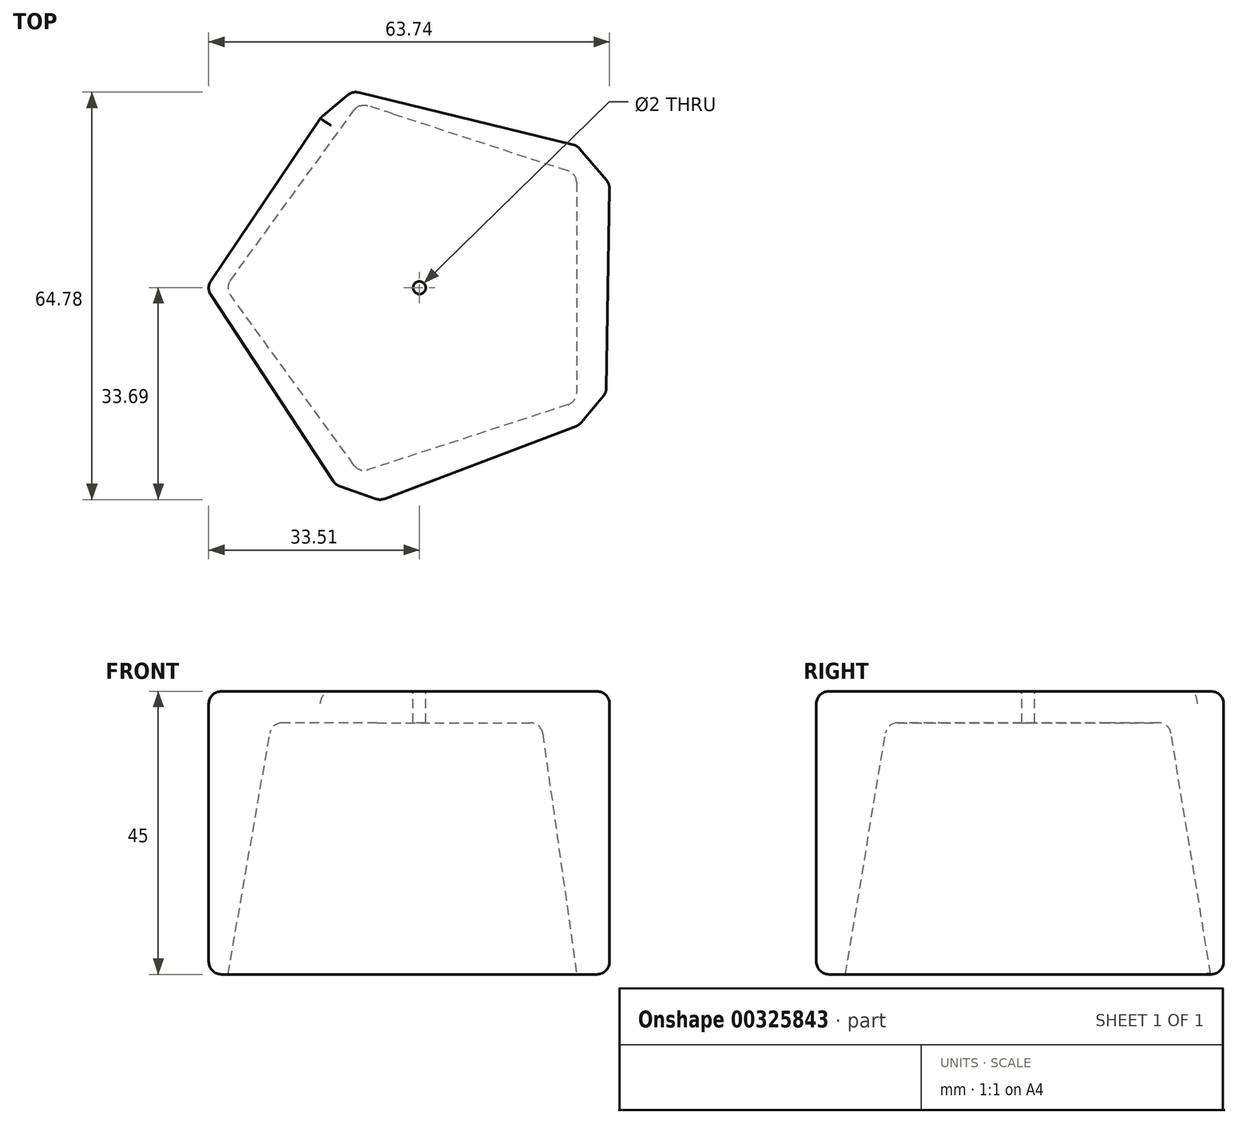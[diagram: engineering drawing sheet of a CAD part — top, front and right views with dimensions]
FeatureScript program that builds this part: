
annotation { "Feature Type Name" : "Feature", "Feature Type Description" : "" }
export const myFeature = defineFeature(function(context is Context, id is Id, definition is map)
    precondition{}
    {
        {
            var Q0;
            Q0=qCreatedBy(makeId("Top.planeOp"),FACE);
            var sketch = newSketch(context, id + "F0", { "sketchPlane" : qUnion([Q0])});
            skLineSegment(sketch, "E0", {"start": v(30.24, 16.51) * mm, "end": v(25.06, 22.6) * mm});
            skLineSegment(sketch, "E1", {"start": v(25.06, 22.6) * mm, "end": v(-10.67, 31.28) * mm});
            skLineSegment(sketch, "E2", {"start": v(-6.22, -33.82) * mm, "end": v(25.44, -21.81) * mm});
            skLineSegment(sketch, "E3", {"start": v(25.44, -21.81) * mm, "end": v(29.72, -16.68) * mm});
            skLineSegment(sketch, "E4", {"start": v(29.72, -16.68) * mm, "end": v(30.24, 16.51) * mm});
            skLineSegment(sketch, "E5", {"start": v(-10.67, 31.28) * mm, "end": v(-15.57, 27.15) * mm});
            skLineSegment(sketch, "E6", {"start": v(-15.57, 27.15) * mm, "end": v(-33.91, 0) * mm});
            skLineSegment(sketch, "E7", {"start": v(-33.91, 0) * mm, "end": v(-13.36, -31.31) * mm});
            skLineSegment(sketch, "E8", {"start": v(-13.36, -31.31) * mm, "end": v(-6.22, -33.82) * mm});
            skSolve(sketch);
        }
        {
            var Q0;
            Q0 = qSketchRegion(id + "F0", true);
            extrude(context, id + "F1", {"entities" : qUnion([Q0]), "depth" : 45 * mm});
        }
        {
            var Q0;
            Q0=qCreatedBy(makeId("Top.planeOp"),FACE);
            var sketch = newSketch(context, id + "F2", { "sketchPlane" : qUnion([Q0])});
            skCircle(sketch, "E9.cCircle", {"center": v(0, 0) * mm, "radius": 25 * mm, "construction": true});
            skLineSegment(sketch, "E9.0", {"start": v(25, 18.16) * mm, "end": v(25, -18.16) * mm});
            skLineSegment(sketch, "E9.1", {"start": v(25, -18.16) * mm, "end": v(-9.55, -29.39) * mm});
            skLineSegment(sketch, "E9.2", {"start": v(-9.55, -29.39) * mm, "end": v(-30.9, 0) * mm});
            skLineSegment(sketch, "E9.3", {"start": v(-30.9, 0) * mm, "end": v(-9.55, 29.39) * mm});
            skLineSegment(sketch, "E9.4", {"start": v(-9.55, 29.39) * mm, "end": v(25, 18.16) * mm});
            skPoint(sketch, "E9.0.midPoint", {"position": v(25, 0) * mm});
            skSolve(sketch);
        }
        {
            var Q0;
            Q0 = qSketchRegion(id + "F2", true);
            extrude(context, id + "F3", {"entities" : qUnion([Q0]), "operationType" : NewBodyOperationType.REMOVE, "depth" : 40 * mm, "hasDraft" : true, "draftAngle" : 8 * degree, "draftPullDirection" : true});
        }
        {
            var Q0;
            Q0=makeQuery(id+"F3.boolean.opBoolean","COPY",EDGE,{"derivedFrom":makeQuery(id+"F3.opExtrude","CAP_EDGE",EDGE,{"disambiguationData":[OSD([sQuery(id+"F2.wireOp",EDGE,"E9.4")])],"isStart":false})});
            var Q1;
            Q1=makeQuery(id+"F3.boolean.opBoolean","COPY",EDGE,{"derivedFrom":makeQuery(id+"F3.opExtrude","SWEPT_EDGE",EDGE,{"disambiguationData":[OSD([sQuery(id+"F2.wireOp",EDGE,"E9.0"),sQuery(id+"F2.wireOp",EDGE,"E9.4")])]})});
            var Q2;
            Q2=makeQuery(id+"F3.boolean.opBoolean","COPY",EDGE,{"derivedFrom":makeQuery(id+"F3.opExtrude","CAP_EDGE",EDGE,{"disambiguationData":[OSD([sQuery(id+"F2.wireOp",EDGE,"E9.0")])],"isStart":false})});
            var Q3;
            Q3=makeQuery(id+"F3.boolean.opBoolean","COPY",EDGE,{"derivedFrom":makeQuery(id+"F3.opExtrude","CAP_EDGE",EDGE,{"disambiguationData":[OSD([sQuery(id+"F2.wireOp",EDGE,"E9.1")])],"isStart":false})});
            var Q4;
            Q4=makeQuery(id+"F3.boolean.opBoolean","COPY",EDGE,{"derivedFrom":makeQuery(id+"F3.opExtrude","CAP_EDGE",EDGE,{"disambiguationData":[OSD([sQuery(id+"F2.wireOp",EDGE,"E9.2")])],"isStart":false})});
            var Q5;
            Q5=makeQuery(id+"F3.boolean.opBoolean","COPY",EDGE,{"derivedFrom":makeQuery(id+"F3.opExtrude","CAP_EDGE",EDGE,{"disambiguationData":[OSD([sQuery(id+"F2.wireOp",EDGE,"E9.3")])],"isStart":false})});
            var Q6;
            Q6=makeQuery(id+"F3.boolean.opBoolean","COPY",EDGE,{"derivedFrom":makeQuery(id+"F3.opExtrude","SWEPT_EDGE",EDGE,{"disambiguationData":[OSD([sQuery(id+"F2.wireOp",EDGE,"E9.3"),sQuery(id+"F2.wireOp",EDGE,"E9.4")])]})});
            var Q7;
            Q7=makeQuery(id+"F3.boolean.opBoolean","COPY",EDGE,{"derivedFrom":makeQuery(id+"F3.opExtrude","SWEPT_EDGE",EDGE,{"disambiguationData":[OSD([sQuery(id+"F2.wireOp",EDGE,"E9.2"),sQuery(id+"F2.wireOp",EDGE,"E9.3")])]})});
            var Q8;
            Q8=makeQuery(id+"F3.boolean.opBoolean","COPY",EDGE,{"derivedFrom":makeQuery(id+"F3.opExtrude","SWEPT_EDGE",EDGE,{"disambiguationData":[OSD([sQuery(id+"F2.wireOp",EDGE,"E9.1"),sQuery(id+"F2.wireOp",EDGE,"E9.2")])]})});
            var Q9;
            Q9=makeQuery(id+"F3.boolean.opBoolean","COPY",EDGE,{"derivedFrom":makeQuery(id+"F3.opExtrude","SWEPT_EDGE",EDGE,{"disambiguationData":[OSD([sQuery(id+"F2.wireOp",EDGE,"E9.0"),sQuery(id+"F2.wireOp",EDGE,"E9.1")])]})});
            fillet(context, id + "F4", {"entities" : qUnion([Q0, Q1, Q2, Q3, Q4, Q5, Q6, Q7, Q8, Q9]), "radius" : 2 * mm, "tangentPropagation" : true, "allowEdgeOverflow" : false});
        }
        {
            var Q0;
            Q0=makeQuery(id+"F1.opExtrude","SWEPT_FACE",FACE,{"disambiguationData":[OSD([sQuery(id+"F0.wireOp",EDGE,"E1")])]});
            var Q1;
            Q1=makeQuery(id+"F1.opExtrude","SWEPT_FACE",FACE,{"disambiguationData":[OSD([sQuery(id+"F0.wireOp",EDGE,"E0")])]});
            var Q2;
            Q2=makeQuery(id+"F1.opExtrude","SWEPT_FACE",FACE,{"disambiguationData":[OSD([sQuery(id+"F0.wireOp",EDGE,"E4")])]});
            var Q3;
            Q3=makeQuery(id+"F1.opExtrude","SWEPT_FACE",FACE,{"disambiguationData":[OSD([sQuery(id+"F0.wireOp",EDGE,"E3")])]});
            var Q4;
            Q4=makeQuery(id+"F1.opExtrude","SWEPT_FACE",FACE,{"disambiguationData":[OSD([sQuery(id+"F0.wireOp",EDGE,"E2")])]});
            var Q5;
            Q5=makeQuery(id+"F1.opExtrude","SWEPT_FACE",FACE,{"disambiguationData":[OSD([sQuery(id+"F0.wireOp",EDGE,"E8")])]});
            var Q6;
            Q6=makeQuery(id+"F1.opExtrude","SWEPT_FACE",FACE,{"disambiguationData":[OSD([sQuery(id+"F0.wireOp",EDGE,"E7")])]});
            var Q7;
            Q7=makeQuery(id+"F1.opExtrude","SWEPT_FACE",FACE,{"disambiguationData":[OSD([sQuery(id+"F0.wireOp",EDGE,"E6")])]});
            var Q8;
            Q8=makeQuery(id+"F1.opExtrude","SWEPT_FACE",FACE,{"disambiguationData":[OSD([sQuery(id+"F0.wireOp",EDGE,"E5")])]});
            fillet(context, id + "F5", {"entities" : qUnion([Q0, Q1, Q2, Q3, Q4, Q5, Q6, Q7, Q8]), "radius" : 2 * mm, "tangentPropagation" : true, "allowEdgeOverflow" : false});
        }
        {
            var Q0;
            Q0=makeQuery(id+"F1.opExtrude","CAP_FACE",FACE,{"disambiguationData":[OSD([sQuery(id+"F0.wireOp",EDGE,"E0"),sQuery(id+"F0.wireOp",EDGE,"E1"),sQuery(id+"F0.wireOp",EDGE,"E2"),sQuery(id+"F0.wireOp",EDGE,"E3"),sQuery(id+"F0.wireOp",EDGE,"E4"),sQuery(id+"F0.wireOp",EDGE,"E5"),sQuery(id+"F0.wireOp",EDGE,"E6"),sQuery(id+"F0.wireOp",EDGE,"E7"),sQuery(id+"F0.wireOp",EDGE,"E8")])],"isStart":false});
            var sketch = newSketch(context, id + "F6", { "sketchPlane" : qUnion([Q0])});
            skCircle(sketch, "E10", {"center": v(0, 0) * mm, "radius": 1 * mm});
            skSolve(sketch);
        }
        {
            var Q0;
            Q0 = qSketchRegion(id + "F6", true);
            extrude(context, id + "F7", {"entities" : qUnion([Q0]), "operationType" : NewBodyOperationType.REMOVE, "endBound" : BoundingType.THROUGH_ALL, "oppositeDirection" : true, "depth" : 10 * mm});
        }
    });
